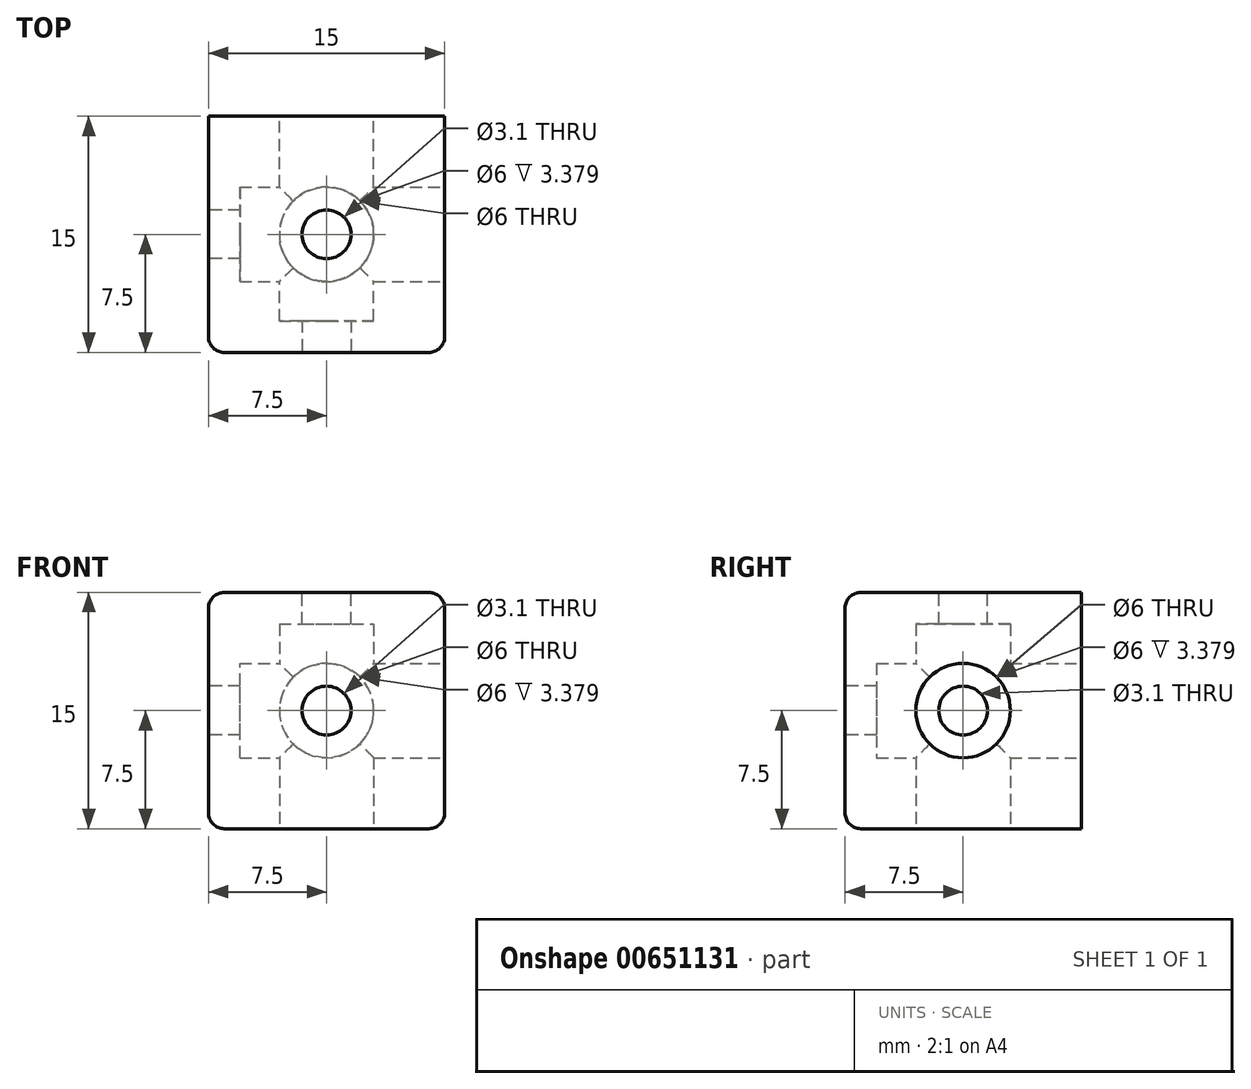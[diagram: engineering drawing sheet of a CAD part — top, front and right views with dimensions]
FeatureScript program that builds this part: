
annotation { "Feature Type Name" : "Feature", "Feature Type Description" : "" }
export const myFeature = defineFeature(function(context is Context, id is Id, definition is map)
    precondition{}
    {
        {
            var Q0;
            Q0=qCreatedBy(makeId("Top.planeOp"),FACE);
            var sketch = newSketch(context, id + "F0", { "sketchPlane" : qUnion([Q0])});
            skLineSegment(sketch, "E0.bottom", {"start": v(0, 0) * mm, "end": v(-15, 0) * mm});
            skLineSegment(sketch, "E0.top", {"start": v(0, 15) * mm, "end": v(-15, 15) * mm});
            skLineSegment(sketch, "E0.left", {"start": v(0, 0) * mm, "end": v(0, 15) * mm});
            skLineSegment(sketch, "E0.right", {"start": v(-15, 0) * mm, "end": v(-15, 15) * mm});
            skSolve(sketch);
        }
        {
            var Q0;
            Q0 = qSketchRegion(id + "F0", true);
            extrude(context, id + "F1", {"entities" : qUnion([Q0]), "depth" : 15 * mm, "offsetDistance" : 25 * mm});
        }
        {
            var Q0;
            Q0=makeQuery(id+"F1.opExtrude","SWEPT_FACE",FACE,{"disambiguationData":[OSD([sQuery(id+"F0.wireOp",EDGE,"E0.bottom")])]});
            var sketch = newSketch(context, id + "F2", { "sketchPlane" : qUnion([Q0])});
            skLineSegment(sketch, "E1", {"start": v(0, 0) * mm, "end": v(-7.5, 0) * mm});
            skLineSegment(sketch, "E2", {"start": v(-7.5, 0) * mm, "end": v(-7.5, 7.5) * mm});
            skCircle(sketch, "E3", {"center": v(-7.5, 7.5) * mm, "radius": 1.55 * mm});
            skSolve(sketch);
        }
        {
            var Q0;
            Q0 = qSketchRegion(id + "F2", true);
            extrude(context, id + "F3", {"entities" : qUnion([Q0]), "operationType" : NewBodyOperationType.REMOVE, "oppositeDirection" : true, "depth" : 25 * mm, "offsetDistance" : 25 * mm});
        }
        {
            var Q0;
            Q0=makeQuery(id+"F1.opExtrude","CAP_FACE",FACE,{"disambiguationData":[OSD([sQuery(id+"F0.wireOp",EDGE,"E0.bottom"),sQuery(id+"F0.wireOp",EDGE,"E0.top"),sQuery(id+"F0.wireOp",EDGE,"E0.left"),sQuery(id+"F0.wireOp",EDGE,"E0.right")])],"isStart":false});
            var sketch = newSketch(context, id + "F4", { "sketchPlane" : qUnion([Q0])});
            skLineSegment(sketch, "E4", {"start": v(0, 0) * mm, "end": v(-7.5, 0) * mm});
            skLineSegment(sketch, "E5", {"start": v(-7.5, 0) * mm, "end": v(-7.5, 7.5) * mm});
            skCircle(sketch, "E6", {"center": v(-7.5, 7.5) * mm, "radius": 1.55 * mm});
            skSolve(sketch);
        }
        {
            var Q0;
            Q0 = qSketchRegion(id + "F4", true);
            extrude(context, id + "F5", {"entities" : qUnion([Q0]), "operationType" : NewBodyOperationType.REMOVE, "oppositeDirection" : true, "depth" : 25 * mm, "offsetDistance" : 25 * mm});
        }
        {
            var Q0;
            Q0=makeQuery(id+"F1.opExtrude","SWEPT_FACE",FACE,{"disambiguationData":[OSD([sQuery(id+"F0.wireOp",EDGE,"E0.left")])]});
            var sketch = newSketch(context, id + "F6", { "sketchPlane" : qUnion([Q0])});
            skLineSegment(sketch, "E7", {"start": v(0, 0) * mm, "end": v(7.5, 0) * mm});
            skLineSegment(sketch, "E8", {"start": v(7.5, 0) * mm, "end": v(7.5, 7.5) * mm});
            skCircle(sketch, "E9", {"center": v(7.5, 7.5) * mm, "radius": 3 * mm});
            skSolve(sketch);
        }
        {
            var Q0;
            Q0 = qSketchRegion(id + "F6", true);
            extrude(context, id + "F7", {"entities" : qUnion([Q0]), "operationType" : NewBodyOperationType.REMOVE, "oppositeDirection" : true, "depth" : 13 * mm, "offsetDistance" : 25 * mm});
        }
        {
            var Q0;
            Q0=makeQuery(id+"F1.opExtrude","SWEPT_FACE",FACE,{"disambiguationData":[OSD([sQuery(id+"F0.wireOp",EDGE,"E0.right")])]});
            var sketch = newSketch(context, id + "F8", { "sketchPlane" : qUnion([Q0])});
            skLineSegment(sketch, "E10", {"start": v(0, 0) * mm, "end": v(-7.5, 0) * mm});
            skLineSegment(sketch, "E11", {"start": v(-7.5, 0) * mm, "end": v(-7.5, 7.5) * mm});
            skCircle(sketch, "E12", {"center": v(-7.5, 7.5) * mm, "radius": 1.55 * mm});
            skSolve(sketch);
        }
        {
            var Q0;
            Q0 = qSketchRegion(id + "F8", true);
            extrude(context, id + "F9", {"entities" : qUnion([Q0]), "operationType" : NewBodyOperationType.REMOVE, "oppositeDirection" : true, "depth" : 25 * mm, "offsetDistance" : 25 * mm});
        }
        {
            var Q0;
            Q0=makeQuery(id+"F1.opExtrude","SWEPT_FACE",FACE,{"disambiguationData":[OSD([sQuery(id+"F0.wireOp",EDGE,"E0.top")])]});
            var sketch = newSketch(context, id + "F10", { "sketchPlane" : qUnion([Q0])});
            skCircle(sketch, "E13", {"center": v(7.5, 7.5) * mm, "radius": 3 * mm});
            skSolve(sketch);
        }
        {
            var Q0;
            Q0 = qSketchRegion(id + "F10", true);
            extrude(context, id + "F11", {"entities" : qUnion([Q0]), "operationType" : NewBodyOperationType.REMOVE, "oppositeDirection" : true, "depth" : 13 * mm, "offsetDistance" : 25 * mm});
        }
        {
            var Q0;
            Q0=makeQuery(id+"F1.opExtrude","CAP_FACE",FACE,{"disambiguationData":[OSD([sQuery(id+"F0.wireOp",EDGE,"E0.bottom"),sQuery(id+"F0.wireOp",EDGE,"E0.top"),sQuery(id+"F0.wireOp",EDGE,"E0.left"),sQuery(id+"F0.wireOp",EDGE,"E0.right")])],"isStart":true});
            var sketch = newSketch(context, id + "F12", { "sketchPlane" : qUnion([Q0])});
            skCircle(sketch, "E14", {"center": v(-7.5, -7.5) * mm, "radius": 3 * mm});
            skSolve(sketch);
        }
        {
            var Q0;
            Q0 = qSketchRegion(id + "F12", true);
            extrude(context, id + "F13", {"entities" : qUnion([Q0]), "operationType" : NewBodyOperationType.REMOVE, "oppositeDirection" : true, "depth" : 13 * mm, "offsetDistance" : 25 * mm});
        }
        {
            var Q0;
            Q0=makeQuery(id+"F1.opExtrude","SWEPT_EDGE",EDGE,{"disambiguationData":[OSD([sQuery(id+"F0.wireOp",EDGE,"E0.bottom"),sQuery(id+"F0.wireOp",EDGE,"E0.right")])]});
            var Q1;
            Q1=makeQuery(id+"F1.opExtrude","CAP_EDGE",EDGE,{"disambiguationData":[OSD([sQuery(id+"F0.wireOp",EDGE,"E0.bottom")])],"isStart":true});
            var Q2;
            Q2=makeQuery(id+"F1.opExtrude","SWEPT_EDGE",EDGE,{"disambiguationData":[OSD([sQuery(id+"F0.wireOp",EDGE,"E0.bottom"),sQuery(id+"F0.wireOp",EDGE,"E0.left")])]});
            var Q3;
            Q3=makeQuery(id+"F1.opExtrude","CAP_EDGE",EDGE,{"disambiguationData":[OSD([sQuery(id+"F0.wireOp",EDGE,"E0.bottom")])],"isStart":false});
            var Q4;
            Q4=makeQuery(id+"F1.opExtrude","CAP_EDGE",EDGE,{"disambiguationData":[OSD([sQuery(id+"F0.wireOp",EDGE,"E0.right")])],"isStart":true});
            var Q5;
            Q5=makeQuery(id+"F1.opExtrude","CAP_EDGE",EDGE,{"disambiguationData":[OSD([sQuery(id+"F0.wireOp",EDGE,"E0.right")])],"isStart":false});
            var Q6;
            Q6=makeQuery(id+"F1.opExtrude","CAP_EDGE",EDGE,{"disambiguationData":[OSD([sQuery(id+"F0.wireOp",EDGE,"E0.left")])],"isStart":false});
            var Q7;
            Q7=makeQuery(id+"F1.opExtrude","CAP_EDGE",EDGE,{"disambiguationData":[OSD([sQuery(id+"F0.wireOp",EDGE,"E0.left")])],"isStart":true});
            fillet(context, id + "F14", {"entities" : qUnion([Q0, Q1, Q2, Q3, Q4, Q5, Q6, Q7]), "radius" : 1 * mm, "tangentPropagation" : true, "allowEdgeOverflow" : false});
        }
    });
